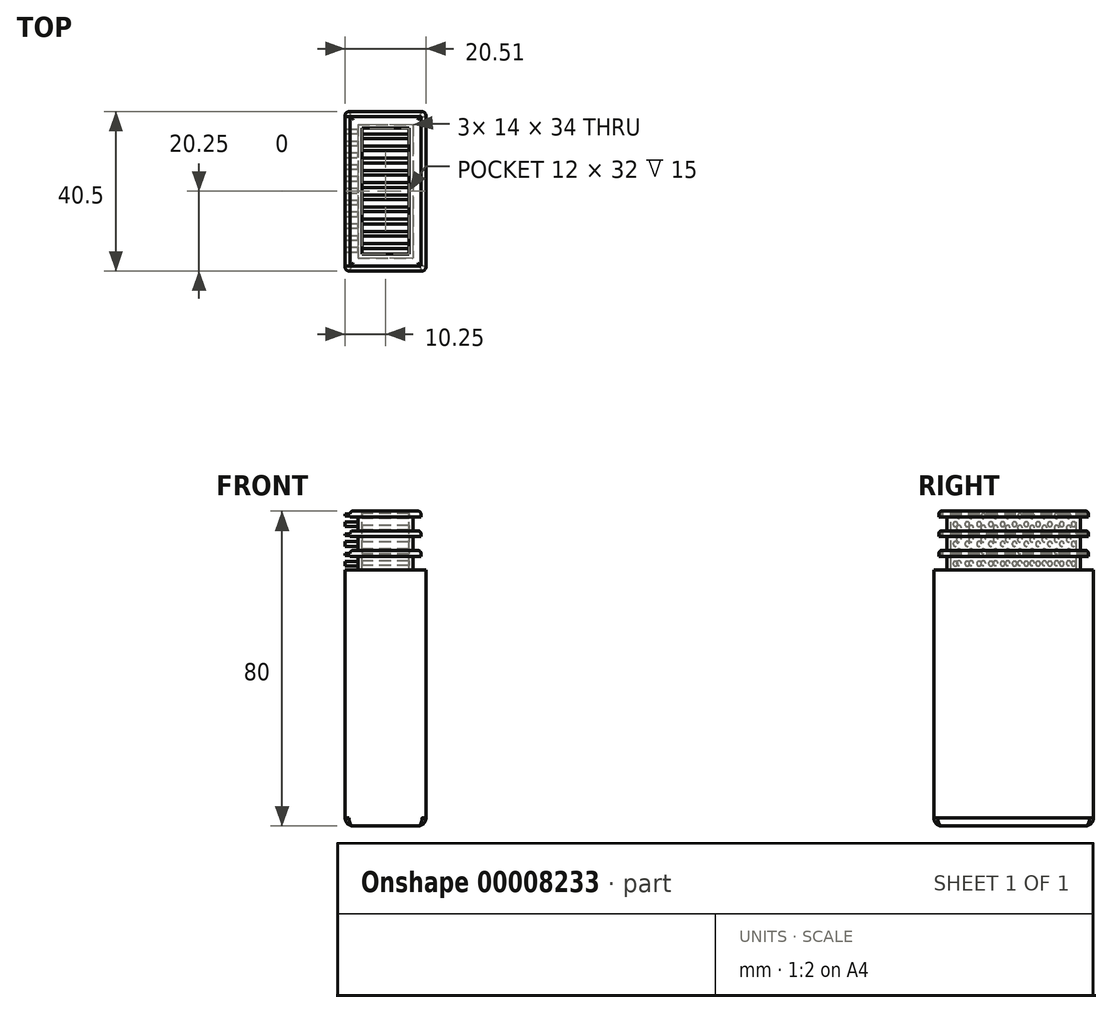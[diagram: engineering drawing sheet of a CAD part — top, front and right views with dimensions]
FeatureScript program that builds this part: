
annotation { "Feature Type Name" : "Feature", "Feature Type Description" : "" }
export const myFeature = defineFeature(function(context is Context, id is Id, definition is map)
    precondition{}
    {
        {
            var Q0;
            Q0=qCreatedBy(makeId("Top.planeOp"),FACE);
            var sketch = newSketch(context, id + "F0", { "sketchPlane" : qUnion([Q0])});
            skLineSegment(sketch, "E0.rect.bottom", {"start": v(10.25, -20.25) * mm, "end": v(-10.25, -20.25) * mm});
            skLineSegment(sketch, "E0.rect.top", {"start": v(10.25, 20.25) * mm, "end": v(-10.25, 20.25) * mm});
            skLineSegment(sketch, "E0.rect.left", {"start": v(10.25, -20.25) * mm, "end": v(10.25, 20.25) * mm});
            skLineSegment(sketch, "E0.rect.right", {"start": v(-10.25, -20.25) * mm, "end": v(-10.25, 20.25) * mm});
            skPoint(sketch, "E0.rect.middle", {"position": v(0, 0) * mm});
            skSolve(sketch);
        }
        {
            var Q0;
            Q0=makeQuery(id+"F0.imprint","IMPRINT",FACE,{"disambiguationData":[TD([[makeQuery(id+"F0.imprint","IMPRINT",EDGE,{"derivedFrom":sQuery(id+"F0.wireOp",EDGE,"E0.rect.bottom")}),-1.0]])]});
            extrude(context, id + "F1", {"entities" : qUnion([Q0]), "depth" : 63 * mm});
        }
        {
            var Q0;
            Q0=makeQuery(id+"F1.opExtrude","CAP_FACE",FACE,{"disambiguationData":[OSD([sQuery(id+"F0.wireOp",EDGE,"E0.rect.bottom"),sQuery(id+"F0.wireOp",EDGE,"E0.rect.top"),sQuery(id+"F0.wireOp",EDGE,"E0.rect.left"),sQuery(id+"F0.wireOp",EDGE,"E0.rect.right")])],"isStart":false});
            var sketch = newSketch(context, id + "F2", { "sketchPlane" : qUnion([Q0])});
            skLineSegment(sketch, "E1.bottom", {"start": v(-7, 17) * mm, "end": v(7, 17) * mm});
            skLineSegment(sketch, "E1.top", {"start": v(-7, -17) * mm, "end": v(7, -17) * mm});
            skLineSegment(sketch, "E1.left", {"start": v(-7, 17) * mm, "end": v(-7, -17) * mm});
            skLineSegment(sketch, "E1.right", {"start": v(7, 17) * mm, "end": v(7, -17) * mm});
            skSolve(sketch);
        }
        {
            var Q0;
            Q0=qSketchRegion(id+"F2",true);
            extrude(context, id + "F3", {"entities" : qUnion([Q0]), "operationType" : NewBodyOperationType.ADD, "depth" : 3.5 * mm});
        }
        {
            var Q0;
            Q0=makeQuery(id+"F3.opExtrude","CAP_FACE",FACE,{"disambiguationData":[OSD([sQuery(id+"F2.wireOp",EDGE,"E1.bottom"),sQuery(id+"F2.wireOp",EDGE,"E1.top"),sQuery(id+"F2.wireOp",EDGE,"E1.left"),sQuery(id+"F2.wireOp",EDGE,"E1.right")])],"isStart":false});
            var sketch = newSketch(context, id + "F4", { "sketchPlane" : qUnion([Q0])});
            skLineSegment(sketch, "E2.bottom", {"start": v(-9, 19) * mm, "end": v(9, 19) * mm});
            skLineSegment(sketch, "E2.top", {"start": v(-9, -19) * mm, "end": v(9, -19) * mm});
            skLineSegment(sketch, "E2.left", {"start": v(-9, 19) * mm, "end": v(-9, -19) * mm});
            skLineSegment(sketch, "E2.right", {"start": v(9, 19) * mm, "end": v(9, -19) * mm});
            skSolve(sketch);
        }
        {
            var Q0;
            Q0=qSketchRegion(id+"F4",true);
            extrude(context, id + "F5", {"entities" : qUnion([Q0]), "operationType" : NewBodyOperationType.ADD, "depth" : 1.5 * mm});
        }
        {
            var Q0;
            Q0=makeQuery(id+"F5.opExtrude","CAP_FACE",FACE,{"disambiguationData":[OSD([sQuery(id+"F4.wireOp",EDGE,"E2.bottom"),sQuery(id+"F4.wireOp",EDGE,"E2.top"),sQuery(id+"F4.wireOp",EDGE,"E2.left"),sQuery(id+"F4.wireOp",EDGE,"E2.right")])],"isStart":false});
            fillet(context, id + "F6", {"entities" : qUnion([Q0]), "radius" : 0.75 * mm, "tangentPropagation" : true, "allowEdgeOverflow" : false});
        }
        {
            var Q0;
            Q0=makeQuery(id+"F5.opExtrude","CAP_FACE",FACE,{"disambiguationData":[OSD([sQuery(id+"F4.wireOp",EDGE,"E2.bottom"),sQuery(id+"F4.wireOp",EDGE,"E2.top"),sQuery(id+"F4.wireOp",EDGE,"E2.left"),sQuery(id+"F4.wireOp",EDGE,"E2.right")])],"isStart":false});
            var sketch = newSketch(context, id + "F7", { "sketchPlane" : qUnion([Q0])});
            skLineSegment(sketch, "E3.rect.bottom", {"start": v(-7, -17) * mm, "end": v(7, -17) * mm});
            skLineSegment(sketch, "E3.rect.top", {"start": v(-7, 17) * mm, "end": v(7, 17) * mm});
            skLineSegment(sketch, "E3.rect.left", {"start": v(-7, -17) * mm, "end": v(-7, 17) * mm});
            skLineSegment(sketch, "E3.rect.right", {"start": v(7, -17) * mm, "end": v(7, 17) * mm});
            skPoint(sketch, "E3.rect.middle", {"position": v(0, 0) * mm});
            skSolve(sketch);
        }
        {
            var Q0;
            Q0=qSketchRegion(id+"F7",true);
            extrude(context, id + "F8", {"entities" : qUnion([Q0]), "operationType" : NewBodyOperationType.ADD, "depth" : 3.5 * mm});
        }
        {
            var Q0;
            Q0=makeQuery(id+"F8.opExtrude","CAP_FACE",FACE,{"disambiguationData":[OSD([sQuery(id+"F7.wireOp",EDGE,"E3.rect.bottom"),sQuery(id+"F7.wireOp",EDGE,"E3.rect.top"),sQuery(id+"F7.wireOp",EDGE,"E3.rect.left"),sQuery(id+"F7.wireOp",EDGE,"E3.rect.right")])],"isStart":false});
            var sketch = newSketch(context, id + "F9", { "sketchPlane" : qUnion([Q0])});
            skLineSegment(sketch, "E4.bottom", {"start": v(-9, 19) * mm, "end": v(9, 19) * mm});
            skLineSegment(sketch, "E4.top", {"start": v(-9, -19) * mm, "end": v(9, -19) * mm});
            skLineSegment(sketch, "E4.left", {"start": v(-9, 19) * mm, "end": v(-9, -19) * mm});
            skLineSegment(sketch, "E4.right", {"start": v(9, 19) * mm, "end": v(9, -19) * mm});
            skSolve(sketch);
        }
        {
            var Q0;
            Q0=qSketchRegion(id+"F9",true);
            extrude(context, id + "F10", {"entities" : qUnion([Q0]), "operationType" : NewBodyOperationType.ADD, "depth" : 1.5 * mm});
        }
        {
            var Q0;
            Q0=makeQuery(id+"F10.opExtrude","CAP_FACE",FACE,{"disambiguationData":[OSD([sQuery(id+"F9.wireOp",EDGE,"E4.bottom"),sQuery(id+"F9.wireOp",EDGE,"E4.top"),sQuery(id+"F9.wireOp",EDGE,"E4.left"),sQuery(id+"F9.wireOp",EDGE,"E4.right")])],"isStart":false});
            var sketch = newSketch(context, id + "F11", { "sketchPlane" : qUnion([Q0])});
            skLineSegment(sketch, "E5.bottom", {"start": v(-7, 17) * mm, "end": v(7, 17) * mm});
            skLineSegment(sketch, "E5.top", {"start": v(-7, -17) * mm, "end": v(7, -17) * mm});
            skLineSegment(sketch, "E5.left", {"start": v(-7, 17) * mm, "end": v(-7, -17) * mm});
            skLineSegment(sketch, "E5.right", {"start": v(7, 17) * mm, "end": v(7, -17) * mm});
            skSolve(sketch);
        }
        {
            var Q0;
            Q0=qSketchRegion(id+"F11",true);
            extrude(context, id + "F12", {"entities" : qUnion([Q0]), "operationType" : NewBodyOperationType.ADD, "depth" : 3.5 * mm});
        }
        {
            var Q0;
            Q0=makeQuery(id+"F12.opExtrude","CAP_FACE",FACE,{"disambiguationData":[OSD([sQuery(id+"F11.wireOp",EDGE,"E5.bottom"),sQuery(id+"F11.wireOp",EDGE,"E5.top"),sQuery(id+"F11.wireOp",EDGE,"E5.left"),sQuery(id+"F11.wireOp",EDGE,"E5.right")])],"isStart":false});
            var sketch = newSketch(context, id + "F13", { "sketchPlane" : qUnion([Q0])});
            skLineSegment(sketch, "E6.bottom", {"start": v(-9, 19) * mm, "end": v(9, 19) * mm});
            skLineSegment(sketch, "E6.top", {"start": v(-9, -19) * mm, "end": v(9, -19) * mm});
            skLineSegment(sketch, "E6.left", {"start": v(-9, 19) * mm, "end": v(-9, -19) * mm});
            skLineSegment(sketch, "E6.right", {"start": v(9, 19) * mm, "end": v(9, -19) * mm});
            skSolve(sketch);
        }
        {
            var Q0;
            Q0=makeQuery(id+"F13.imprint","IMPRINT",FACE,{"disambiguationData":[TD([[makeQuery(id+"F13.imprint","IMPRINT",EDGE,{"derivedFrom":sQuery(id+"F13.wireOp",EDGE,"E6.bottom")}),-1.0]])]});
            var Q1;
            Q1=makeQuery(id+"F13.imprint","IMPRINT",FACE,{"disambiguationData":[TD([[makeQuery(id+"F13.imprint","IMPRINT",EDGE,{"derivedFrom":makeQuery(id+"F12.opExtrude","CAP_EDGE",EDGE,{"disambiguationData":[OSD([sQuery(id+"F11.wireOp",EDGE,"E5.bottom")])],"isStart":false})}),-1.0]])]});
            extrude(context, id + "F14", {"entities" : qUnion([Q0, Q1]), "operationType" : NewBodyOperationType.ADD, "depth" : 1.5 * mm});
        }
        {
            var Q0;
            Q0=makeQuery(id+"F10.opExtrude","CAP_EDGE",EDGE,{"disambiguationData":[OSD([sQuery(id+"F9.wireOp",EDGE,"E4.bottom")])],"isStart":false});
            var Q1;
            Q1=makeQuery(id+"F10.opExtrude","CAP_EDGE",EDGE,{"disambiguationData":[OSD([sQuery(id+"F9.wireOp",EDGE,"E4.left")])],"isStart":false});
            var Q2;
            Q2=makeQuery(id+"F10.opExtrude","CAP_EDGE",EDGE,{"disambiguationData":[OSD([sQuery(id+"F9.wireOp",EDGE,"E4.right")])],"isStart":false});
            var Q3;
            Q3=makeQuery(id+"F10.opExtrude","CAP_EDGE",EDGE,{"disambiguationData":[OSD([sQuery(id+"F9.wireOp",EDGE,"E4.top")])],"isStart":false});
            fillet(context, id + "F15", {"entities" : qUnion([Q0, Q1, Q2, Q3]), "radius" : 0.75 * mm, "tangentPropagation" : true, "allowEdgeOverflow" : false});
        }
        {
            var Q0;
            Q0=makeQuery(id+"F14.opExtrude","CAP_EDGE",EDGE,{"disambiguationData":[OSD([sQuery(id+"F13.wireOp",EDGE,"E6.left")])],"isStart":false});
            var Q1;
            Q1=makeQuery(id+"F14.opExtrude","CAP_EDGE",EDGE,{"disambiguationData":[OSD([sQuery(id+"F13.wireOp",EDGE,"E6.top")])],"isStart":false});
            var Q2;
            Q2=makeQuery(id+"F14.opExtrude","CAP_EDGE",EDGE,{"disambiguationData":[OSD([sQuery(id+"F13.wireOp",EDGE,"E6.right")])],"isStart":false});
            var Q3;
            Q3=makeQuery(id+"F14.opExtrude","CAP_EDGE",EDGE,{"disambiguationData":[OSD([sQuery(id+"F13.wireOp",EDGE,"E6.bottom")])],"isStart":false});
            fillet(context, id + "F16", {"entities" : qUnion([Q0, Q1, Q2, Q3]), "radius" : 0.75 * mm, "tangentPropagation" : true, "allowEdgeOverflow" : false});
        }
        {
            var Q0;
            Q0=makeQuery(id+"F14.opExtrude","CAP_FACE",FACE,{"disambiguationData":[OSD([sQuery(id+"F13.wireOp",EDGE,"E6.bottom"),sQuery(id+"F13.wireOp",EDGE,"E6.top"),sQuery(id+"F13.wireOp",EDGE,"E6.left"),sQuery(id+"F13.wireOp",EDGE,"E6.right")])],"isStart":false});
            var sketch = newSketch(context, id + "F17", { "sketchPlane" : qUnion([Q0])});
            skLineSegment(sketch, "E7.bottom", {"start": v(-6, 16) * mm, "end": v(6, 16) * mm});
            skLineSegment(sketch, "E7.top", {"start": v(-6, -16) * mm, "end": v(6, -16) * mm});
            skLineSegment(sketch, "E7.left", {"start": v(-6, 16) * mm, "end": v(-6, -16) * mm});
            skLineSegment(sketch, "E7.right", {"start": v(6, 16) * mm, "end": v(6, -16) * mm});
            skSolve(sketch);
        }
        {
            var Q0;
            Q0=makeQuery(id+"F17.imprint","IMPRINT",FACE,{"disambiguationData":[TD([[makeQuery(id+"F17.imprint","IMPRINT",EDGE,{"derivedFrom":sQuery(id+"F17.wireOp",EDGE,"E7.bottom")}),-1.0]])]});
            var Q1;
            Q1=makeQuery(id+"F1.opExtrude","CAP_FACE",FACE,{"disambiguationData":[OSD([sQuery(id+"F0.wireOp",EDGE,"E0.rect.bottom"),sQuery(id+"F0.wireOp",EDGE,"E0.rect.top"),sQuery(id+"F0.wireOp",EDGE,"E0.rect.left"),sQuery(id+"F0.wireOp",EDGE,"E0.rect.right")])],"isStart":false});
            extrude(context, id + "F18", {"entities" : qUnion([Q0]), "operationType" : NewBodyOperationType.REMOVE, "oppositeDirection" : true, "endBoundEntity" : qUnion([Q1]), "depth" : 15 * mm});
        }
        {
            var Q0;
            Q0=makeQuery(id+"F1.opExtrude","SWEPT_EDGE",EDGE,{"disambiguationData":[OSD([sQuery(id+"F0.wireOp",EDGE,"E0.rect.bottom"),sQuery(id+"F0.wireOp",EDGE,"E0.rect.left")])]});
            var Q1;
            Q1=makeQuery(id+"F1.opExtrude","SWEPT_EDGE",EDGE,{"disambiguationData":[OSD([sQuery(id+"F0.wireOp",EDGE,"E0.rect.top"),sQuery(id+"F0.wireOp",EDGE,"E0.rect.left")])]});
            var Q2;
            Q2=makeQuery(id+"F1.opExtrude","SWEPT_EDGE",EDGE,{"disambiguationData":[OSD([sQuery(id+"F0.wireOp",EDGE,"E0.rect.top"),sQuery(id+"F0.wireOp",EDGE,"E0.rect.right")])]});
            var Q3;
            Q3=makeQuery(id+"F1.opExtrude","SWEPT_EDGE",EDGE,{"disambiguationData":[OSD([sQuery(id+"F0.wireOp",EDGE,"E0.rect.bottom"),sQuery(id+"F0.wireOp",EDGE,"E0.rect.right")])]});
            fillet(context, id + "F19", {"entities" : qUnion([Q0, Q1, Q2, Q3]), "radius" : 1 * mm, "tangentPropagation" : true, "allowEdgeOverflow" : false});
        }
        {
            var Q0;
            Q0=makeQuery(id+"F1.opExtrude","CAP_FACE",FACE,{"disambiguationData":[OSD([sQuery(id+"F0.wireOp",EDGE,"E0.rect.bottom"),sQuery(id+"F0.wireOp",EDGE,"E0.rect.top"),sQuery(id+"F0.wireOp",EDGE,"E0.rect.left"),sQuery(id+"F0.wireOp",EDGE,"E0.rect.right")])],"isStart":true});
            var sketch = newSketch(context, id + "F20", { "sketchPlane" : qUnion([Q0])});
            skLineSegment(sketch, "E8.bottom", {"start": v(-7.25, 17.25) * mm, "end": v(-4.75, 17.25) * mm});
            skLineSegment(sketch, "E8.top", {"start": v(-7.25, 14.25) * mm, "end": v(-4.75, 14.25) * mm});
            skLineSegment(sketch, "E8.left", {"start": v(-7.25, 17.25) * mm, "end": v(-7.25, 14.25) * mm});
            skLineSegment(sketch, "E8.right", {"start": v(-4.75, 17.25) * mm, "end": v(-4.75, 14.25) * mm});
            skLineSegment(sketch, "E9.1.0.0", {"start": v(-3.25, 17.25) * mm, "end": v(-0.75, 17.25) * mm});
            skLineSegment(sketch, "E9.1.0.1", {"start": v(-0.75, 17.25) * mm, "end": v(-0.75, 14.25) * mm});
            skLineSegment(sketch, "E9.1.0.2", {"start": v(-3.25, 17.25) * mm, "end": v(-3.25, 14.25) * mm});
            skLineSegment(sketch, "E9.1.0.3", {"start": v(-3.25, 14.25) * mm, "end": v(-0.75, 14.25) * mm});
            skLineSegment(sketch, "E9.2.0.0", {"start": v(0.75, 17.25) * mm, "end": v(3.25, 17.25) * mm});
            skLineSegment(sketch, "E9.2.0.1", {"start": v(3.25, 17.25) * mm, "end": v(3.25, 14.25) * mm});
            skLineSegment(sketch, "E9.2.0.2", {"start": v(0.75, 17.25) * mm, "end": v(0.75, 14.25) * mm});
            skLineSegment(sketch, "E9.2.0.3", {"start": v(0.75, 14.25) * mm, "end": v(3.25, 14.25) * mm});
            skLineSegment(sketch, "E9.3.0.0", {"start": v(4.75, 17.25) * mm, "end": v(7.25, 17.25) * mm});
            skLineSegment(sketch, "E9.3.0.1", {"start": v(7.25, 17.25) * mm, "end": v(7.25, 14.25) * mm});
            skLineSegment(sketch, "E9.3.0.2", {"start": v(4.75, 17.25) * mm, "end": v(4.75, 14.25) * mm});
            skLineSegment(sketch, "E9.3.0.3", {"start": v(4.75, 14.25) * mm, "end": v(7.25, 14.25) * mm});
            skLineSegment(sketch, "E9.direction1", {"start": v(-7.25, 17.25) * mm, "end": v(-3.25, 17.25) * mm, "construction": true});
            skLineSegment(sketch, "E10.1.0.0", {"start": v(-7.24, 12.75) * mm, "end": v(-7.24, 9.75) * mm});
            skLineSegment(sketch, "E10.1.0.1", {"start": v(-3.24, 12.75) * mm, "end": v(-3.24, 9.75) * mm});
            skLineSegment(sketch, "E10.1.0.2", {"start": v(-3.24, 9.75) * mm, "end": v(-0.74, 9.75) * mm});
            skLineSegment(sketch, "E10.1.0.3", {"start": v(4.76, 9.75) * mm, "end": v(7.26, 9.75) * mm});
            skLineSegment(sketch, "E10.1.0.4", {"start": v(-7.24, 9.75) * mm, "end": v(-4.74, 9.75) * mm});
            skLineSegment(sketch, "E10.1.0.5", {"start": v(-7.24, 12.75) * mm, "end": v(-4.74, 12.75) * mm});
            skLineSegment(sketch, "E10.1.0.6", {"start": v(4.76, 12.75) * mm, "end": v(4.76, 9.75) * mm});
            skLineSegment(sketch, "E10.1.0.7", {"start": v(-0.74, 12.75) * mm, "end": v(-0.74, 9.75) * mm});
            skLineSegment(sketch, "E10.1.0.8", {"start": v(-7.24, 12.75) * mm, "end": v(-3.24, 12.75) * mm, "construction": true});
            skLineSegment(sketch, "E10.1.0.9", {"start": v(0.76, 9.75) * mm, "end": v(3.26, 9.75) * mm});
            skLineSegment(sketch, "E10.1.0.10", {"start": v(4.76, 12.75) * mm, "end": v(7.26, 12.75) * mm});
            skLineSegment(sketch, "E10.1.0.11", {"start": v(0.76, 12.75) * mm, "end": v(3.26, 12.75) * mm});
            skLineSegment(sketch, "E10.1.0.12", {"start": v(3.26, 12.75) * mm, "end": v(3.26, 9.75) * mm});
            skLineSegment(sketch, "E10.1.0.13", {"start": v(7.26, 12.75) * mm, "end": v(7.26, 9.75) * mm});
            skLineSegment(sketch, "E10.1.0.14", {"start": v(0.76, 12.75) * mm, "end": v(0.76, 9.75) * mm});
            skLineSegment(sketch, "E10.1.0.15", {"start": v(-3.24, 12.75) * mm, "end": v(-0.74, 12.75) * mm});
            skLineSegment(sketch, "E10.1.0.16", {"start": v(-4.74, 12.75) * mm, "end": v(-4.74, 9.75) * mm});
            skLineSegment(sketch, "E10.2.0.0", {"start": v(-7.22, 8.25) * mm, "end": v(-7.22, 5.25) * mm});
            skLineSegment(sketch, "E10.2.0.1", {"start": v(-3.22, 8.25) * mm, "end": v(-3.22, 5.25) * mm});
            skLineSegment(sketch, "E10.2.0.2", {"start": v(-3.22, 5.25) * mm, "end": v(-0.72, 5.25) * mm});
            skLineSegment(sketch, "E10.2.0.3", {"start": v(4.78, 5.25) * mm, "end": v(7.28, 5.25) * mm});
            skLineSegment(sketch, "E10.2.0.4", {"start": v(-7.22, 5.25) * mm, "end": v(-4.72, 5.25) * mm});
            skLineSegment(sketch, "E10.2.0.5", {"start": v(-7.22, 8.25) * mm, "end": v(-4.72, 8.25) * mm});
            skLineSegment(sketch, "E10.2.0.6", {"start": v(4.78, 8.25) * mm, "end": v(4.78, 5.25) * mm});
            skLineSegment(sketch, "E10.2.0.7", {"start": v(-0.72, 8.25) * mm, "end": v(-0.72, 5.25) * mm});
            skLineSegment(sketch, "E10.2.0.8", {"start": v(-7.22, 8.25) * mm, "end": v(-3.22, 8.25) * mm, "construction": true});
            skLineSegment(sketch, "E10.2.0.9", {"start": v(0.78, 5.25) * mm, "end": v(3.28, 5.25) * mm});
            skLineSegment(sketch, "E10.2.0.10", {"start": v(4.78, 8.25) * mm, "end": v(7.28, 8.25) * mm});
            skLineSegment(sketch, "E10.2.0.11", {"start": v(0.78, 8.25) * mm, "end": v(3.28, 8.25) * mm});
            skLineSegment(sketch, "E10.2.0.12", {"start": v(3.28, 8.25) * mm, "end": v(3.28, 5.25) * mm});
            skLineSegment(sketch, "E10.2.0.13", {"start": v(7.28, 8.25) * mm, "end": v(7.28, 5.25) * mm});
            skLineSegment(sketch, "E10.2.0.14", {"start": v(0.78, 8.25) * mm, "end": v(0.78, 5.25) * mm});
            skLineSegment(sketch, "E10.2.0.15", {"start": v(-3.22, 8.25) * mm, "end": v(-0.72, 8.25) * mm});
            skLineSegment(sketch, "E10.2.0.16", {"start": v(-4.72, 8.25) * mm, "end": v(-4.72, 5.25) * mm});
            skLineSegment(sketch, "E10.3.0.0", {"start": v(-7.21, 3.75) * mm, "end": v(-7.21, 0.75) * mm});
            skLineSegment(sketch, "E10.3.0.1", {"start": v(-3.21, 3.75) * mm, "end": v(-3.21, 0.75) * mm});
            skLineSegment(sketch, "E10.3.0.2", {"start": v(-3.21, 0.75) * mm, "end": v(-0.71, 0.75) * mm});
            skLineSegment(sketch, "E10.3.0.3", {"start": v(4.79, 0.75) * mm, "end": v(7.29, 0.75) * mm});
            skLineSegment(sketch, "E10.3.0.4", {"start": v(-7.21, 0.75) * mm, "end": v(-4.71, 0.75) * mm});
            skLineSegment(sketch, "E10.3.0.5", {"start": v(-7.21, 3.75) * mm, "end": v(-4.71, 3.75) * mm});
            skLineSegment(sketch, "E10.3.0.6", {"start": v(4.79, 3.75) * mm, "end": v(4.79, 0.75) * mm});
            skLineSegment(sketch, "E10.3.0.7", {"start": v(-0.71, 3.75) * mm, "end": v(-0.71, 0.75) * mm});
            skLineSegment(sketch, "E10.3.0.8", {"start": v(-7.21, 3.75) * mm, "end": v(-3.21, 3.75) * mm, "construction": true});
            skLineSegment(sketch, "E10.3.0.9", {"start": v(0.79, 0.75) * mm, "end": v(3.29, 0.75) * mm});
            skLineSegment(sketch, "E10.3.0.10", {"start": v(4.79, 3.75) * mm, "end": v(7.29, 3.75) * mm});
            skLineSegment(sketch, "E10.3.0.11", {"start": v(0.79, 3.75) * mm, "end": v(3.29, 3.75) * mm});
            skLineSegment(sketch, "E10.3.0.12", {"start": v(3.29, 3.75) * mm, "end": v(3.29, 0.75) * mm});
            skLineSegment(sketch, "E10.3.0.13", {"start": v(7.29, 3.75) * mm, "end": v(7.29, 0.75) * mm});
            skLineSegment(sketch, "E10.3.0.14", {"start": v(0.79, 3.75) * mm, "end": v(0.79, 0.75) * mm});
            skLineSegment(sketch, "E10.3.0.15", {"start": v(-3.21, 3.75) * mm, "end": v(-0.71, 3.75) * mm});
            skLineSegment(sketch, "E10.3.0.16", {"start": v(-4.71, 3.75) * mm, "end": v(-4.71, 0.75) * mm});
            skLineSegment(sketch, "E10.4.0.0", {"start": v(-7.2, -0.75) * mm, "end": v(-7.2, -3.75) * mm});
            skLineSegment(sketch, "E10.4.0.1", {"start": v(-3.2, -0.75) * mm, "end": v(-3.2, -3.75) * mm});
            skLineSegment(sketch, "E10.4.0.2", {"start": v(-3.2, -3.75) * mm, "end": v(-0.7, -3.75) * mm});
            skLineSegment(sketch, "E10.4.0.3", {"start": v(4.8, -3.75) * mm, "end": v(7.3, -3.75) * mm});
            skLineSegment(sketch, "E10.4.0.4", {"start": v(-7.2, -3.75) * mm, "end": v(-4.7, -3.75) * mm});
            skLineSegment(sketch, "E10.4.0.5", {"start": v(-7.2, -0.75) * mm, "end": v(-4.7, -0.75) * mm});
            skLineSegment(sketch, "E10.4.0.6", {"start": v(4.8, -0.75) * mm, "end": v(4.8, -3.75) * mm});
            skLineSegment(sketch, "E10.4.0.7", {"start": v(-0.7, -0.75) * mm, "end": v(-0.7, -3.75) * mm});
            skLineSegment(sketch, "E10.4.0.8", {"start": v(-7.2, -0.75) * mm, "end": v(-3.2, -0.75) * mm, "construction": true});
            skLineSegment(sketch, "E10.4.0.9", {"start": v(0.8, -3.75) * mm, "end": v(3.3, -3.75) * mm});
            skLineSegment(sketch, "E10.4.0.10", {"start": v(4.8, -0.75) * mm, "end": v(7.3, -0.75) * mm});
            skLineSegment(sketch, "E10.4.0.11", {"start": v(0.8, -0.75) * mm, "end": v(3.3, -0.75) * mm});
            skLineSegment(sketch, "E10.4.0.12", {"start": v(3.3, -0.75) * mm, "end": v(3.3, -3.75) * mm});
            skLineSegment(sketch, "E10.4.0.13", {"start": v(7.3, -0.75) * mm, "end": v(7.3, -3.75) * mm});
            skLineSegment(sketch, "E10.4.0.14", {"start": v(0.8, -0.75) * mm, "end": v(0.8, -3.75) * mm});
            skLineSegment(sketch, "E10.4.0.15", {"start": v(-3.2, -0.75) * mm, "end": v(-0.7, -0.75) * mm});
            skLineSegment(sketch, "E10.4.0.16", {"start": v(-4.7, -0.75) * mm, "end": v(-4.7, -3.75) * mm});
            skLineSegment(sketch, "E10.5.0.0", {"start": v(-7.18, -5.25) * mm, "end": v(-7.18, -8.25) * mm});
            skLineSegment(sketch, "E10.5.0.1", {"start": v(-3.18, -5.25) * mm, "end": v(-3.18, -8.25) * mm});
            skLineSegment(sketch, "E10.5.0.2", {"start": v(-3.18, -8.25) * mm, "end": v(-0.68, -8.25) * mm});
            skLineSegment(sketch, "E10.5.0.3", {"start": v(4.82, -8.25) * mm, "end": v(7.32, -8.25) * mm});
            skLineSegment(sketch, "E10.5.0.4", {"start": v(-7.18, -8.25) * mm, "end": v(-4.68, -8.25) * mm});
            skLineSegment(sketch, "E10.5.0.5", {"start": v(-7.18, -5.25) * mm, "end": v(-4.68, -5.25) * mm});
            skLineSegment(sketch, "E10.5.0.6", {"start": v(4.82, -5.25) * mm, "end": v(4.82, -8.25) * mm});
            skLineSegment(sketch, "E10.5.0.7", {"start": v(-0.68, -5.25) * mm, "end": v(-0.68, -8.25) * mm});
            skLineSegment(sketch, "E10.5.0.8", {"start": v(-7.18, -5.25) * mm, "end": v(-3.18, -5.25) * mm, "construction": true});
            skLineSegment(sketch, "E10.5.0.9", {"start": v(0.82, -8.25) * mm, "end": v(3.32, -8.25) * mm});
            skLineSegment(sketch, "E10.5.0.10", {"start": v(4.82, -5.25) * mm, "end": v(7.32, -5.25) * mm});
            skLineSegment(sketch, "E10.5.0.11", {"start": v(0.82, -5.25) * mm, "end": v(3.32, -5.25) * mm});
            skLineSegment(sketch, "E10.5.0.12", {"start": v(3.32, -5.25) * mm, "end": v(3.32, -8.25) * mm});
            skLineSegment(sketch, "E10.5.0.13", {"start": v(7.32, -5.25) * mm, "end": v(7.32, -8.25) * mm});
            skLineSegment(sketch, "E10.5.0.14", {"start": v(0.82, -5.25) * mm, "end": v(0.82, -8.25) * mm});
            skLineSegment(sketch, "E10.5.0.15", {"start": v(-3.18, -5.25) * mm, "end": v(-0.68, -5.25) * mm});
            skLineSegment(sketch, "E10.5.0.16", {"start": v(-4.68, -5.25) * mm, "end": v(-4.68, -8.25) * mm});
            skLineSegment(sketch, "E10.6.0.0", {"start": v(-7.17, -9.75) * mm, "end": v(-7.17, -12.75) * mm});
            skLineSegment(sketch, "E10.6.0.1", {"start": v(-3.17, -9.75) * mm, "end": v(-3.17, -12.75) * mm});
            skLineSegment(sketch, "E10.6.0.2", {"start": v(-3.17, -12.75) * mm, "end": v(-0.67, -12.75) * mm});
            skLineSegment(sketch, "E10.6.0.3", {"start": v(4.83, -12.75) * mm, "end": v(7.33, -12.75) * mm});
            skLineSegment(sketch, "E10.6.0.4", {"start": v(-7.17, -12.75) * mm, "end": v(-4.67, -12.75) * mm});
            skLineSegment(sketch, "E10.6.0.5", {"start": v(-7.17, -9.75) * mm, "end": v(-4.67, -9.75) * mm});
            skLineSegment(sketch, "E10.6.0.6", {"start": v(4.83, -9.75) * mm, "end": v(4.83, -12.75) * mm});
            skLineSegment(sketch, "E10.6.0.7", {"start": v(-0.67, -9.75) * mm, "end": v(-0.67, -12.75) * mm});
            skLineSegment(sketch, "E10.6.0.8", {"start": v(-7.17, -9.75) * mm, "end": v(-3.17, -9.75) * mm, "construction": true});
            skLineSegment(sketch, "E10.6.0.9", {"start": v(0.83, -12.75) * mm, "end": v(3.33, -12.75) * mm});
            skLineSegment(sketch, "E10.6.0.10", {"start": v(4.83, -9.75) * mm, "end": v(7.33, -9.75) * mm});
            skLineSegment(sketch, "E10.6.0.11", {"start": v(0.83, -9.75) * mm, "end": v(3.33, -9.75) * mm});
            skLineSegment(sketch, "E10.6.0.12", {"start": v(3.33, -9.75) * mm, "end": v(3.33, -12.75) * mm});
            skLineSegment(sketch, "E10.6.0.13", {"start": v(7.33, -9.75) * mm, "end": v(7.33, -12.75) * mm});
            skLineSegment(sketch, "E10.6.0.14", {"start": v(0.83, -9.75) * mm, "end": v(0.83, -12.75) * mm});
            skLineSegment(sketch, "E10.6.0.15", {"start": v(-3.17, -9.75) * mm, "end": v(-0.67, -9.75) * mm});
            skLineSegment(sketch, "E10.6.0.16", {"start": v(-4.67, -9.75) * mm, "end": v(-4.67, -12.75) * mm});
            skLineSegment(sketch, "E10.7.0.0", {"start": v(-7.16, -14.25) * mm, "end": v(-7.16, -17.25) * mm});
            skLineSegment(sketch, "E10.7.0.1", {"start": v(-3.16, -14.25) * mm, "end": v(-3.16, -17.25) * mm});
            skLineSegment(sketch, "E10.7.0.2", {"start": v(-3.16, -17.25) * mm, "end": v(-0.66, -17.25) * mm});
            skLineSegment(sketch, "E10.7.0.3", {"start": v(4.84, -17.25) * mm, "end": v(7.34, -17.25) * mm});
            skLineSegment(sketch, "E10.7.0.4", {"start": v(-7.16, -17.25) * mm, "end": v(-4.66, -17.25) * mm});
            skLineSegment(sketch, "E10.7.0.5", {"start": v(-7.16, -14.25) * mm, "end": v(-4.66, -14.25) * mm});
            skLineSegment(sketch, "E10.7.0.6", {"start": v(4.84, -14.25) * mm, "end": v(4.84, -17.25) * mm});
            skLineSegment(sketch, "E10.7.0.7", {"start": v(-0.66, -14.25) * mm, "end": v(-0.66, -17.25) * mm});
            skLineSegment(sketch, "E10.7.0.8", {"start": v(-7.16, -14.25) * mm, "end": v(-3.16, -14.25) * mm, "construction": true});
            skLineSegment(sketch, "E10.7.0.9", {"start": v(0.84, -17.25) * mm, "end": v(3.34, -17.25) * mm});
            skLineSegment(sketch, "E10.7.0.10", {"start": v(4.84, -14.25) * mm, "end": v(7.34, -14.25) * mm});
            skLineSegment(sketch, "E10.7.0.11", {"start": v(0.84, -14.25) * mm, "end": v(3.34, -14.25) * mm});
            skLineSegment(sketch, "E10.7.0.12", {"start": v(3.34, -14.25) * mm, "end": v(3.34, -17.25) * mm});
            skLineSegment(sketch, "E10.7.0.13", {"start": v(7.34, -14.25) * mm, "end": v(7.34, -17.25) * mm});
            skLineSegment(sketch, "E10.7.0.14", {"start": v(0.84, -14.25) * mm, "end": v(0.84, -17.25) * mm});
            skLineSegment(sketch, "E10.7.0.15", {"start": v(-3.16, -14.25) * mm, "end": v(-0.66, -14.25) * mm});
            skLineSegment(sketch, "E10.7.0.16", {"start": v(-4.66, -14.25) * mm, "end": v(-4.66, -17.25) * mm});
            skLineSegment(sketch, "E10.direction1", {"start": v(-7.25, 14.25) * mm, "end": v(-7.24, 9.75) * mm, "construction": true});
            skSolve(sketch);
        }
        {
            var Q0;
            Q0=makeQuery(id+"F1.opExtrude","CAP_FACE",FACE,{"disambiguationData":[OSD([sQuery(id+"F0.wireOp",EDGE,"E0.rect.bottom"),sQuery(id+"F0.wireOp",EDGE,"E0.rect.top"),sQuery(id+"F0.wireOp",EDGE,"E0.rect.left"),sQuery(id+"F0.wireOp",EDGE,"E0.rect.right")])],"isStart":true});
            var sketch = newSketch(context, id + "F21", { "sketchPlane" : qUnion([Q0])});
            skLineSegment(sketch, "E11.bottom", {"start": v(-10.24, 20.25) * mm, "end": v(10.26, 20.25) * mm});
            skLineSegment(sketch, "E11.top", {"start": v(-10.24, -20.25) * mm, "end": v(10.26, -20.25) * mm});
            skLineSegment(sketch, "E11.left", {"start": v(-10.24, 20.25) * mm, "end": v(-10.24, -20.25) * mm});
            skLineSegment(sketch, "E11.right", {"start": v(10.26, 20.25) * mm, "end": v(10.26, -20.25) * mm});
            skSolve(sketch);
        }
        {
            var Q0;
            Q0=qSketchRegion(id+"F21",true);
            extrude(context, id + "F22", {"entities" : qUnion([Q0]), "operationType" : NewBodyOperationType.ADD, "depth" : 2 * mm});
        }
        {
            var Q0;
            Q0=makeQuery(id+"F22.opExtrude","CAP_EDGE",EDGE,{"disambiguationData":[OSD([sQuery(id+"F21.wireOp",EDGE,"E11.left")])],"isStart":false});
            var Q1;
            Q1=makeQuery(id+"F22.opExtrude","CAP_EDGE",EDGE,{"disambiguationData":[OSD([sQuery(id+"F21.wireOp",EDGE,"E11.bottom")])],"isStart":false});
            var Q2;
            Q2=makeQuery(id+"F22.opExtrude","CAP_EDGE",EDGE,{"disambiguationData":[OSD([sQuery(id+"F21.wireOp",EDGE,"E11.right")])],"isStart":false});
            var Q3;
            Q3=makeQuery(id+"F22.opExtrude","CAP_EDGE",EDGE,{"disambiguationData":[OSD([sQuery(id+"F21.wireOp",EDGE,"E11.top")])],"isStart":false});
            fillet(context, id + "F23", {"entities" : qUnion([Q0, Q1, Q2, Q3]), "radius" : 2 * mm, "tangentPropagation" : true, "allowEdgeOverflow" : false});
        }
        {
            var Q0;
            Q0=makeQuery(id+"F23.opFillet","BLEND_EDGE",EDGE,{"blendedFrom":[makeQuery(id+"F22.opExtrude","CAP_EDGE",EDGE,{"disambiguationData":[OSD([sQuery(id+"F21.wireOp",EDGE,"E11.bottom")])],"isStart":false}),makeQuery(id+"F22.opExtrude","CAP_EDGE",EDGE,{"disambiguationData":[OSD([sQuery(id+"F21.wireOp",EDGE,"E11.left")])],"isStart":false})],"blendedInto":[]});
            var Q1;
            Q1=makeQuery(id+"F23.opFillet","BLEND_EDGE",EDGE,{"blendedFrom":[makeQuery(id+"F22.opExtrude","CAP_EDGE",EDGE,{"disambiguationData":[OSD([sQuery(id+"F21.wireOp",EDGE,"E11.top")])],"isStart":false}),makeQuery(id+"F22.opExtrude","CAP_EDGE",EDGE,{"disambiguationData":[OSD([sQuery(id+"F21.wireOp",EDGE,"E11.left")])],"isStart":false})],"blendedInto":[]});
            var Q2;
            Q2=makeQuery(id+"F23.opFillet","BLEND_EDGE",EDGE,{"blendedFrom":[makeQuery(id+"F22.opExtrude","CAP_EDGE",EDGE,{"disambiguationData":[OSD([sQuery(id+"F21.wireOp",EDGE,"E11.bottom")])],"isStart":false}),makeQuery(id+"F22.opExtrude","CAP_EDGE",EDGE,{"disambiguationData":[OSD([sQuery(id+"F21.wireOp",EDGE,"E11.right")])],"isStart":false})],"blendedInto":[]});
            var Q3;
            Q3=makeQuery(id+"F23.opFillet","BLEND_EDGE",EDGE,{"blendedFrom":[makeQuery(id+"F22.opExtrude","CAP_EDGE",EDGE,{"disambiguationData":[OSD([sQuery(id+"F21.wireOp",EDGE,"E11.top")])],"isStart":false}),makeQuery(id+"F22.opExtrude","CAP_EDGE",EDGE,{"disambiguationData":[OSD([sQuery(id+"F21.wireOp",EDGE,"E11.right")])],"isStart":false})],"blendedInto":[]});
            fillet(context, id + "F24", {"entities" : qUnion([Q0, Q1, Q2, Q3]), "radius" : 1 * mm, "tangentPropagation" : true, "allowEdgeOverflow" : false});
        }
        {
            var Q0;
            Q0=makeQuery(id+"F18.boolean.opBoolean","COPY",FACE,{"derivedFrom":makeQuery(id+"F18.opExtrude","SWEPT_FACE",FACE,{"disambiguationData":[OSD([sQuery(id+"F17.wireOp",EDGE,"E7.left")])]})});
            var sketch = newSketch(context, id + "F25", { "sketchPlane" : qUnion([Q0])});
            skCircle(sketch, "E12.9.3.0", {"center": v(14, 67.75) * mm, "radius": 0.6 * mm});
            skCircle(sketch, "E12.1.3.0", {"center": v(-10.8, 67.75) * mm, "radius": 0.6 * mm});
            skCircle(sketch, "E12.5.0.0", {"center": v(1.6, 76.75) * mm, "radius": 0.6 * mm});
            skCircle(sketch, "E12.3.1.0", {"center": v(-4.6, 73.75) * mm, "radius": 0.6 * mm});
            skCircle(sketch, "E12.8.1.0", {"center": v(10.9, 73.75) * mm, "radius": 0.6 * mm});
            skCircle(sketch, "E12.6.2.0", {"center": v(4.7, 70.75) * mm, "radius": 0.6 * mm});
            skCircle(sketch, "E12.1.2.0", {"center": v(-10.8, 70.75) * mm, "radius": 0.6 * mm});
            skCircle(sketch, "E12.2.3.0", {"center": v(-7.7, 67.75) * mm, "radius": 0.6 * mm});
            skCircle(sketch, "E12.4.2.0", {"center": v(-1.5, 70.75) * mm, "radius": 0.6 * mm});
            skCircle(sketch, "E12.7.3.0", {"center": v(7.8, 67.75) * mm, "radius": 0.6 * mm});
            skCircle(sketch, "E12.2.4.0", {"center": v(-7.7, 64.75) * mm, "radius": 0.6 * mm});
            skCircle(sketch, "E12.3.0.0", {"center": v(-4.6, 76.75) * mm, "radius": 0.6 * mm});
            skCircle(sketch, "E13", {"center": v(-13.9, 76.75) * mm, "radius": 0.6 * mm});
            skCircle(sketch, "E12.0.1.0", {"center": v(-13.9, 73.75) * mm, "radius": 0.6 * mm});
            skCircle(sketch, "E12.0.2.0", {"center": v(-13.9, 70.75) * mm, "radius": 0.6 * mm});
            skCircle(sketch, "E12.4.4.0", {"center": v(-1.5, 64.75) * mm, "radius": 0.6 * mm});
            skCircle(sketch, "E12.8.0.0", {"center": v(10.9, 76.75) * mm, "radius": 0.6 * mm});
            skCircle(sketch, "E12.1.4.0", {"center": v(-10.8, 64.75) * mm, "radius": 0.6 * mm});
            skCircle(sketch, "E12.0.3.0", {"center": v(-13.9, 67.75) * mm, "radius": 0.6 * mm});
            skCircle(sketch, "E12.0.4.0", {"center": v(-13.9, 64.75) * mm, "radius": 0.6 * mm});
            skCircle(sketch, "E12.1.0.0", {"center": v(-10.8, 76.75) * mm, "radius": 0.6 * mm});
            skCircle(sketch, "E12.1.1.0", {"center": v(-10.8, 73.75) * mm, "radius": 0.6 * mm});
            skCircle(sketch, "E12.2.0.0", {"center": v(-7.7, 76.75) * mm, "radius": 0.6 * mm});
            skCircle(sketch, "E12.2.1.0", {"center": v(-7.7, 73.75) * mm, "radius": 0.6 * mm});
            skCircle(sketch, "E12.2.2.0", {"center": v(-7.7, 70.75) * mm, "radius": 0.6 * mm});
            skCircle(sketch, "E12.5.3.0", {"center": v(1.6, 67.75) * mm, "radius": 0.6 * mm});
            skCircle(sketch, "E12.8.4.0", {"center": v(10.9, 64.75) * mm, "radius": 0.6 * mm});
            skCircle(sketch, "E12.9.0.0", {"center": v(14, 76.75) * mm, "radius": 0.6 * mm});
            skCircle(sketch, "E12.5.4.0", {"center": v(1.6, 64.75) * mm, "radius": 0.6 * mm});
            skCircle(sketch, "E12.4.1.0", {"center": v(-1.5, 73.75) * mm, "radius": 0.6 * mm});
            skCircle(sketch, "E12.7.2.0", {"center": v(7.8, 70.75) * mm, "radius": 0.6 * mm});
            skCircle(sketch, "E12.9.4.0", {"center": v(14, 64.75) * mm, "radius": 0.6 * mm});
            skCircle(sketch, "E12.4.3.0", {"center": v(-1.5, 67.75) * mm, "radius": 0.6 * mm});
            skCircle(sketch, "E12.3.2.0", {"center": v(-4.6, 70.75) * mm, "radius": 0.6 * mm});
            skCircle(sketch, "E12.7.4.0", {"center": v(7.8, 64.75) * mm, "radius": 0.6 * mm});
            skCircle(sketch, "E12.6.3.0", {"center": v(4.7, 67.75) * mm, "radius": 0.6 * mm});
            skCircle(sketch, "E12.8.3.0", {"center": v(10.9, 67.75) * mm, "radius": 0.6 * mm});
            skCircle(sketch, "E12.5.2.0", {"center": v(1.6, 70.75) * mm, "radius": 0.6 * mm});
            skCircle(sketch, "E12.6.0.0", {"center": v(4.7, 76.75) * mm, "radius": 0.6 * mm});
            skCircle(sketch, "E12.9.1.0", {"center": v(14, 73.75) * mm, "radius": 0.6 * mm});
            skCircle(sketch, "E12.7.1.0", {"center": v(7.8, 73.75) * mm, "radius": 0.6 * mm});
            skCircle(sketch, "E12.4.0.0", {"center": v(-1.5, 76.75) * mm, "radius": 0.6 * mm});
            skCircle(sketch, "E12.9.2.0", {"center": v(14, 70.75) * mm, "radius": 0.6 * mm});
            skCircle(sketch, "E12.8.2.0", {"center": v(10.9, 70.75) * mm, "radius": 0.6 * mm});
            skCircle(sketch, "E12.7.0.0", {"center": v(7.8, 76.75) * mm, "radius": 0.6 * mm});
            skCircle(sketch, "E12.6.1.0", {"center": v(4.7, 73.75) * mm, "radius": 0.6 * mm});
            skCircle(sketch, "E12.6.4.0", {"center": v(4.7, 64.75) * mm, "radius": 0.6 * mm});
            skCircle(sketch, "E12.5.1.0", {"center": v(1.6, 73.75) * mm, "radius": 0.6 * mm});
            skCircle(sketch, "E12.3.3.0", {"center": v(-4.6, 67.75) * mm, "radius": 0.6 * mm});
            skCircle(sketch, "E12.3.4.0", {"center": v(-4.6, 64.75) * mm, "radius": 0.6 * mm});
            skLineSegment(sketch, "E12.direction1", {"start": v(-13.9, 76.75) * mm, "end": v(-10.8, 76.75) * mm, "construction": true});
            skLineSegment(sketch, "E12.direction2", {"start": v(-13.9, 76.75) * mm, "end": v(-13.9, 73.75) * mm, "construction": true});
            skSolve(sketch);
        }
        {
            var Q0;
            Q0=makeQuery(id+"F1.opExtrude","SWEPT_FACE",FACE,{"disambiguationData":[OSD([sQuery(id+"F0.wireOp",EDGE,"E0.rect.right")])]});
            cPlane(context, id + "F26", {"entities" : qUnion([Q0]), "cplaneType" : CPlaneType.OFFSET, "offset" : 0 * mm, "width" : 150 * mm, "height" : 150 * mm});
        }
        {
            var Q0;
            Q0 = qSketchRegion(id + "F25", true);
            extrude(context, id + "F27", {"entities" : qUnion([Q0]), "operationType" : NewBodyOperationType.ADD, "depth" : 13 * mm});
        }
        {
            var Q0;
            Q0=makeQuery(id+"F5.opExtrude","SWEPT_FACE",FACE,{"disambiguationData":[OSD([sQuery(id+"F4.wireOp",EDGE,"E2.left")])]});
            var sketch = newSketch(context, id + "F28", { "sketchPlane" : qUnion([Q0])});
            skLineSegment(sketch, "E14.bottom", {"start": v(-19, 67.25) * mm, "end": v(19, 67.25) * mm});
            skLineSegment(sketch, "E14.top", {"start": v(-19, 66.75) * mm, "end": v(19, 66.75) * mm});
            skLineSegment(sketch, "E14.left", {"start": v(-19, 67.25) * mm, "end": v(-19, 66.75) * mm});
            skLineSegment(sketch, "E14.right", {"start": v(19, 67.25) * mm, "end": v(19, 66.75) * mm});
            skLineSegment(sketch, "E15.0.1.0", {"start": v(-19, 71.75) * mm, "end": v(19, 71.75) * mm});
            skLineSegment(sketch, "E15.0.1.1", {"start": v(-19, 72.25) * mm, "end": v(19, 72.25) * mm});
            skLineSegment(sketch, "E15.0.1.2", {"start": v(19, 72.25) * mm, "end": v(19, 71.75) * mm});
            skLineSegment(sketch, "E15.0.1.3", {"start": v(-19, 72.25) * mm, "end": v(-19, 71.75) * mm});
            skLineSegment(sketch, "E15.0.2.0", {"start": v(-19, 76.75) * mm, "end": v(19, 76.75) * mm});
            skLineSegment(sketch, "E15.0.2.1", {"start": v(-19, 77.25) * mm, "end": v(19, 77.25) * mm});
            skLineSegment(sketch, "E15.0.2.2", {"start": v(19, 77.25) * mm, "end": v(19, 76.75) * mm});
            skLineSegment(sketch, "E15.0.2.3", {"start": v(-19, 77.25) * mm, "end": v(-19, 76.75) * mm});
            skLineSegment(sketch, "E15.direction1", {"start": v(-19, 66.75) * mm, "end": v(6, 66.75) * mm, "construction": true});
            skLineSegment(sketch, "E15.direction2", {"start": v(-19, 66.75) * mm, "end": v(-19, 71.75) * mm, "construction": true});
            skSolve(sketch);
        }
        {
            var Q0;
            Q0 = qSketchRegion(id + "F28", true);
            var Q1;
            Q1=qCreatedBy(id+"F26.planeOp",FACE);
            extrude(context, id + "F29", {"entities" : qUnion([Q0]), "operationType" : NewBodyOperationType.ADD, "endBound" : BoundingType.UP_TO_SURFACE, "endBoundEntityFace" : qUnion([Q1]), "depth" : 1.26 * mm});
        }
        {
            var Q0;
            Q0=makeQuery(id+"F12.opExtrude","SWEPT_FACE",FACE,{"disambiguationData":[OSD([sQuery(id+"F11.wireOp",EDGE,"E5.left")])]});
            var sketch = newSketch(context, id + "F30", { "sketchPlane" : qUnion([Q0])});
            skCircle(sketch, "E16", {"center": v(-15.21, 74.66) * mm, "radius": 0.6 * mm});
            skCircle(sketch, "E17.0.1.0", {"center": v(-15.21, 69.66) * mm, "radius": 0.6 * mm});
            skCircle(sketch, "E17.0.2.0", {"center": v(-15.21, 64.66) * mm, "radius": 0.6 * mm});
            skCircle(sketch, "E17.1.0.0", {"center": v(-12.21, 74.66) * mm, "radius": 0.6 * mm});
            skCircle(sketch, "E17.1.1.0", {"center": v(-12.21, 69.66) * mm, "radius": 0.6 * mm});
            skCircle(sketch, "E17.1.2.0", {"center": v(-12.21, 64.66) * mm, "radius": 0.6 * mm});
            skCircle(sketch, "E17.2.0.0", {"center": v(-9.21, 74.66) * mm, "radius": 0.6 * mm});
            skCircle(sketch, "E17.2.1.0", {"center": v(-9.21, 69.66) * mm, "radius": 0.6 * mm});
            skCircle(sketch, "E17.2.2.0", {"center": v(-9.21, 64.66) * mm, "radius": 0.6 * mm});
            skCircle(sketch, "E17.3.0.0", {"center": v(-6.21, 74.66) * mm, "radius": 0.6 * mm});
            skCircle(sketch, "E17.3.1.0", {"center": v(-6.21, 69.66) * mm, "radius": 0.6 * mm});
            skCircle(sketch, "E17.3.2.0", {"center": v(-6.21, 64.66) * mm, "radius": 0.6 * mm});
            skCircle(sketch, "E17.4.0.0", {"center": v(-3.21, 74.66) * mm, "radius": 0.6 * mm});
            skCircle(sketch, "E17.4.1.0", {"center": v(-3.21, 69.66) * mm, "radius": 0.6 * mm});
            skCircle(sketch, "E17.4.2.0", {"center": v(-3.21, 64.66) * mm, "radius": 0.6 * mm});
            skCircle(sketch, "E17.5.0.0", {"center": v(-0.21, 74.66) * mm, "radius": 0.6 * mm});
            skCircle(sketch, "E17.5.1.0", {"center": v(-0.21, 69.66) * mm, "radius": 0.6 * mm});
            skCircle(sketch, "E17.5.2.0", {"center": v(-0.21, 64.66) * mm, "radius": 0.6 * mm});
            skCircle(sketch, "E17.6.0.0", {"center": v(2.79, 74.66) * mm, "radius": 0.6 * mm});
            skCircle(sketch, "E17.6.1.0", {"center": v(2.79, 69.66) * mm, "radius": 0.6 * mm});
            skCircle(sketch, "E17.6.2.0", {"center": v(2.79, 64.66) * mm, "radius": 0.6 * mm});
            skCircle(sketch, "E17.7.0.0", {"center": v(5.79, 74.66) * mm, "radius": 0.6 * mm});
            skCircle(sketch, "E17.7.1.0", {"center": v(5.79, 69.66) * mm, "radius": 0.6 * mm});
            skCircle(sketch, "E17.7.2.0", {"center": v(5.79, 64.66) * mm, "radius": 0.6 * mm});
            skCircle(sketch, "E17.8.0.0", {"center": v(8.79, 74.66) * mm, "radius": 0.6 * mm});
            skCircle(sketch, "E17.8.1.0", {"center": v(8.79, 69.66) * mm, "radius": 0.6 * mm});
            skCircle(sketch, "E17.8.2.0", {"center": v(8.79, 64.66) * mm, "radius": 0.6 * mm});
            skCircle(sketch, "E17.9.0.0", {"center": v(11.79, 74.66) * mm, "radius": 0.6 * mm});
            skCircle(sketch, "E17.9.1.0", {"center": v(11.79, 69.66) * mm, "radius": 0.6 * mm});
            skCircle(sketch, "E17.9.2.0", {"center": v(11.79, 64.66) * mm, "radius": 0.6 * mm});
            skCircle(sketch, "E17.10.0.0", {"center": v(14.79, 74.66) * mm, "radius": 0.6 * mm});
            skCircle(sketch, "E17.10.1.0", {"center": v(14.79, 69.66) * mm, "radius": 0.6 * mm});
            skCircle(sketch, "E17.10.2.0", {"center": v(14.79, 64.66) * mm, "radius": 0.6 * mm});
            skLineSegment(sketch, "E17.direction1", {"start": v(-15.21, 74.66) * mm, "end": v(-12.21, 74.66) * mm, "construction": true});
            skLineSegment(sketch, "E17.direction2", {"start": v(-15.21, 74.66) * mm, "end": v(-15.21, 69.66) * mm, "construction": true});
            skSolve(sketch);
        }
        {
            var Q0;
            Q0 = qSketchRegion(id + "F30", true);
            var Q1;
            Q1=qCreatedBy(id+"F26.planeOp",FACE);
            extrude(context, id + "F31", {"entities" : qUnion([Q0]), "operationType" : NewBodyOperationType.ADD, "endBound" : BoundingType.UP_TO_SURFACE, "endBoundEntityFace" : qUnion([Q1]), "depth" : 25 * mm});
        }
    });
